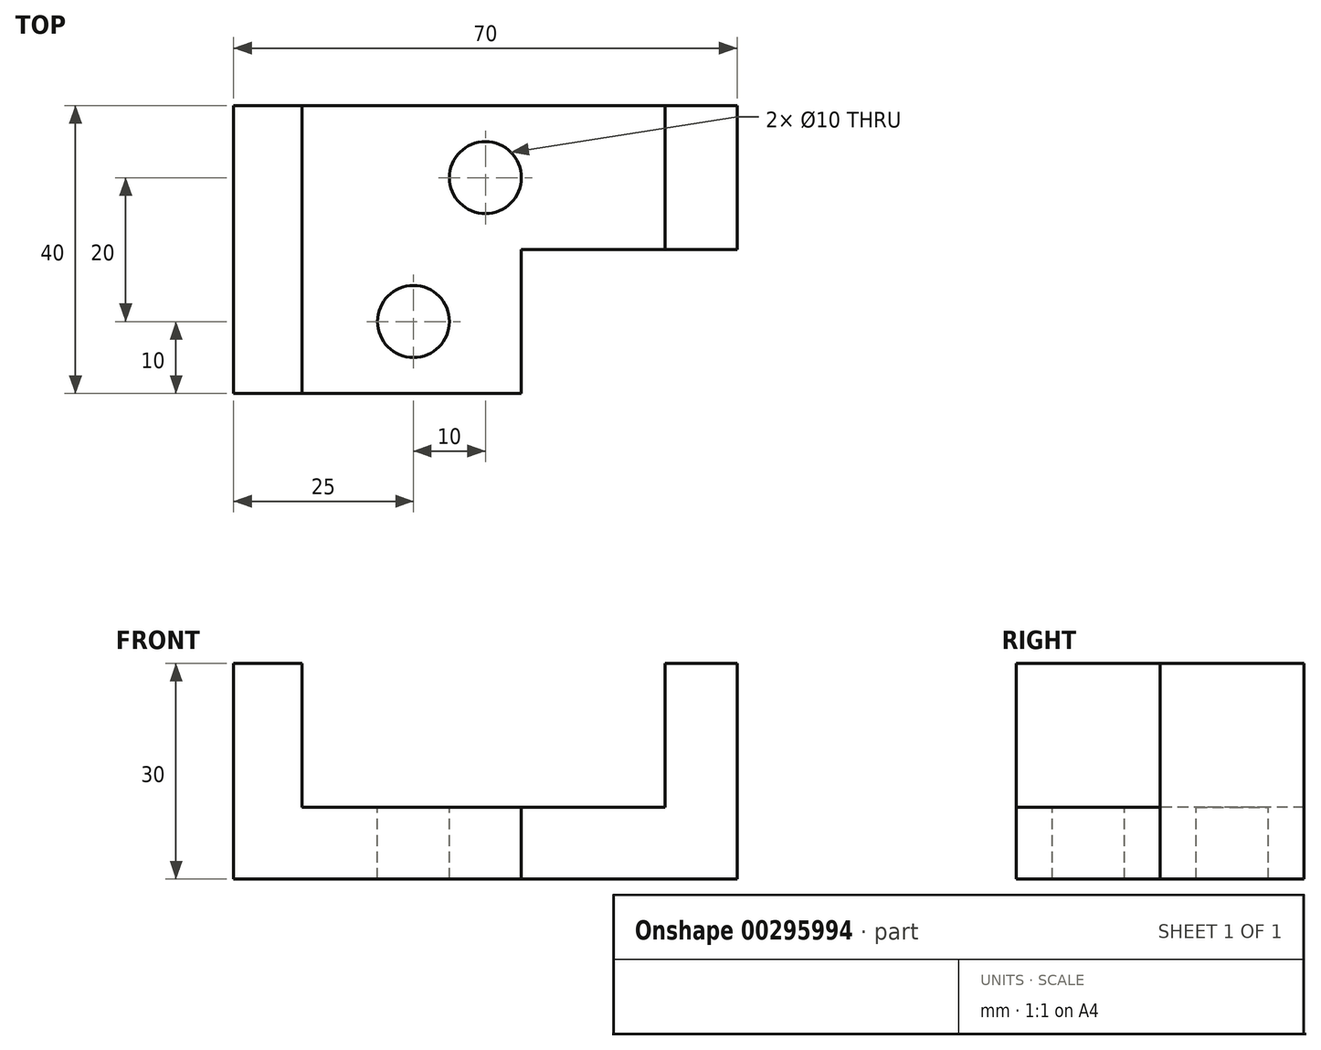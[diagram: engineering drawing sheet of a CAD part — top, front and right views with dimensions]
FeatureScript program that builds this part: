
annotation { "Feature Type Name" : "Feature", "Feature Type Description" : "" }
export const myFeature = defineFeature(function(context is Context, id is Id, definition is map)
    precondition{}
    {
        {
            var Q0;
            Q0=qCreatedBy(makeId("Top.planeOp"),FACE);
            var sketch = newSketch(context, id + "F0", { "sketchPlane" : qUnion([Q0])});
            skLineSegment(sketch, "E0", {"start": v(0, 0) * mm, "end": v(40, 0) * mm});
            skLineSegment(sketch, "E1", {"start": v(40, 0) * mm, "end": v(40, 20) * mm});
            skLineSegment(sketch, "E2", {"start": v(40, 20) * mm, "end": v(70, 20) * mm});
            skLineSegment(sketch, "E3", {"start": v(70, 20) * mm, "end": v(70, 40) * mm});
            skLineSegment(sketch, "E4", {"start": v(70, 40) * mm, "end": v(0, 40) * mm});
            skLineSegment(sketch, "E5", {"start": v(0, 40) * mm, "end": v(0, 0) * mm});
            skSolve(sketch);
        }
        {
            var Q0;
            Q0=makeQuery(id+"F0.imprint","IMPRINT",FACE,{"disambiguationData":[TD([[makeQuery(id+"F0.imprint","IMPRINT",EDGE,{"derivedFrom":sQuery(id+"F0.wireOp",EDGE,"E0")}),1.0]])]});
            extrude(context, id + "F1", {"entities" : qUnion([Q0]), "depth" : 10 * mm});
        }
        {
            var Q0;
            Q0=makeQuery(id+"F1.opExtrude","CAP_FACE",FACE,{"disambiguationData":[OSD([sQuery(id+"F0.wireOp",EDGE,"E0"),sQuery(id+"F0.wireOp",EDGE,"E1"),sQuery(id+"F0.wireOp",EDGE,"E2"),sQuery(id+"F0.wireOp",EDGE,"E3"),sQuery(id+"F0.wireOp",EDGE,"E4"),sQuery(id+"F0.wireOp",EDGE,"E5")])],"isStart":false});
            var sketch = newSketch(context, id + "F2", { "sketchPlane" : qUnion([Q0])});
            skLineSegment(sketch, "E6.bottom", {"start": v(0, 40) * mm, "end": v(9.5, 40) * mm});
            skLineSegment(sketch, "E6.top", {"start": v(0, 0) * mm, "end": v(9.5, 0) * mm});
            skLineSegment(sketch, "E6.left", {"start": v(0, 40) * mm, "end": v(0, 0) * mm});
            skLineSegment(sketch, "E6.right", {"start": v(9.5, 40) * mm, "end": v(9.5, 0) * mm});
            skSolve(sketch);
        }
        {
            var Q0;
            Q0=makeQuery(id+"F2.imprint","IMPRINT",FACE,{"disambiguationData":[TD([[makeQuery(id+"F2.imprint","IMPRINT",EDGE,{"derivedFrom":sQuery(id+"F2.wireOp",EDGE,"E6.bottom")}),1.0]])]});
            extrude(context, id + "F3", {"entities" : qUnion([Q0]), "operationType" : NewBodyOperationType.ADD, "depth" : 20 * mm});
        }
        {
            var Q0;
            Q0=makeQuery(id+"F1.opExtrude","CAP_FACE",FACE,{"disambiguationData":[OSD([sQuery(id+"F0.wireOp",EDGE,"E0"),sQuery(id+"F0.wireOp",EDGE,"E1"),sQuery(id+"F0.wireOp",EDGE,"E2"),sQuery(id+"F0.wireOp",EDGE,"E3"),sQuery(id+"F0.wireOp",EDGE,"E4"),sQuery(id+"F0.wireOp",EDGE,"E5")])],"isStart":false});
            var sketch = newSketch(context, id + "F4", { "sketchPlane" : qUnion([Q0])});
            skLineSegment(sketch, "E7.bottom", {"start": v(70, 40) * mm, "end": v(60, 40) * mm});
            skLineSegment(sketch, "E7.top", {"start": v(70, 20) * mm, "end": v(60, 20) * mm});
            skLineSegment(sketch, "E7.left", {"start": v(70, 40) * mm, "end": v(70, 20) * mm});
            skLineSegment(sketch, "E7.right", {"start": v(60, 40) * mm, "end": v(60, 20) * mm});
            skSolve(sketch);
        }
        {
            var Q0;
            Q0=makeQuery(id+"F4.imprint","IMPRINT",FACE,{"disambiguationData":[TD([[makeQuery(id+"F4.imprint","IMPRINT",EDGE,{"derivedFrom":sQuery(id+"F4.wireOp",EDGE,"E7.bottom")}),1.0]])]});
            extrude(context, id + "F5", {"entities" : qUnion([Q0]), "operationType" : NewBodyOperationType.ADD, "depth" : 20 * mm});
        }
        {
            var Q0;
            Q0=makeQuery(id+"F1.opExtrude","CAP_FACE",FACE,{"disambiguationData":[OSD([sQuery(id+"F0.wireOp",EDGE,"E0"),sQuery(id+"F0.wireOp",EDGE,"E1"),sQuery(id+"F0.wireOp",EDGE,"E2"),sQuery(id+"F0.wireOp",EDGE,"E3"),sQuery(id+"F0.wireOp",EDGE,"E4"),sQuery(id+"F0.wireOp",EDGE,"E5")])],"isStart":false});
            var sketch = newSketch(context, id + "F6", { "sketchPlane" : qUnion([Q0])});
            skLineSegment(sketch, "E8", {"start": v(40, 0) * mm, "end": v(25, 0) * mm});
            skLineSegment(sketch, "E9", {"start": v(40, 0) * mm, "end": v(40, 10) * mm});
            skCircle(sketch, "E10", {"center": v(25, 10) * mm, "radius": 5 * mm});
            skLineSegment(sketch, "E11", {"start": v(40, 0) * mm, "end": v(40, 10) * mm, "construction": true});
            skSolve(sketch);
        }
        {
            var Q0;
            Q0=makeQuery(id+"F6.imprint","IMPRINT",FACE,{"disambiguationData":[TD([[makeQuery(id+"F6.imprint","IMPRINT",EDGE,{"derivedFrom":sQuery(id+"F6.wireOp",EDGE,"E10")}),1.0]])]});
            extrude(context, id + "F7", {"entities" : qUnion([Q0]), "operationType" : NewBodyOperationType.REMOVE, "endBound" : BoundingType.THROUGH_ALL, "oppositeDirection" : true, "depth" : 25 * mm});
        }
        {
            var Q0;
            Q0=makeQuery(id+"F1.opExtrude","CAP_FACE",FACE,{"disambiguationData":[OSD([sQuery(id+"F0.wireOp",EDGE,"E0"),sQuery(id+"F0.wireOp",EDGE,"E1"),sQuery(id+"F0.wireOp",EDGE,"E2"),sQuery(id+"F0.wireOp",EDGE,"E3"),sQuery(id+"F0.wireOp",EDGE,"E4"),sQuery(id+"F0.wireOp",EDGE,"E5")])],"isStart":false});
            var sketch = newSketch(context, id + "F8", { "sketchPlane" : qUnion([Q0])});
            skLineSegment(sketch, "E12", {"start": v(0, 40) * mm, "end": v(0, 30) * mm, "construction": true});
            skLineSegment(sketch, "E13", {"start": v(0, 40) * mm, "end": v(35, 40) * mm});
            skCircle(sketch, "E14", {"center": v(35, 30) * mm, "radius": 5 * mm});
            skSolve(sketch);
        }
        {
            var Q0;
            Q0=makeQuery(id+"F8.imprint","IMPRINT",FACE,{"disambiguationData":[TD([[makeQuery(id+"F8.imprint","IMPRINT",EDGE,{"derivedFrom":sQuery(id+"F8.wireOp",EDGE,"E14")}),1.0]])]});
            extrude(context, id + "F9", {"entities" : qUnion([Q0]), "operationType" : NewBodyOperationType.REMOVE, "endBound" : BoundingType.THROUGH_ALL, "oppositeDirection" : true, "depth" : 25 * mm});
        }
    });
